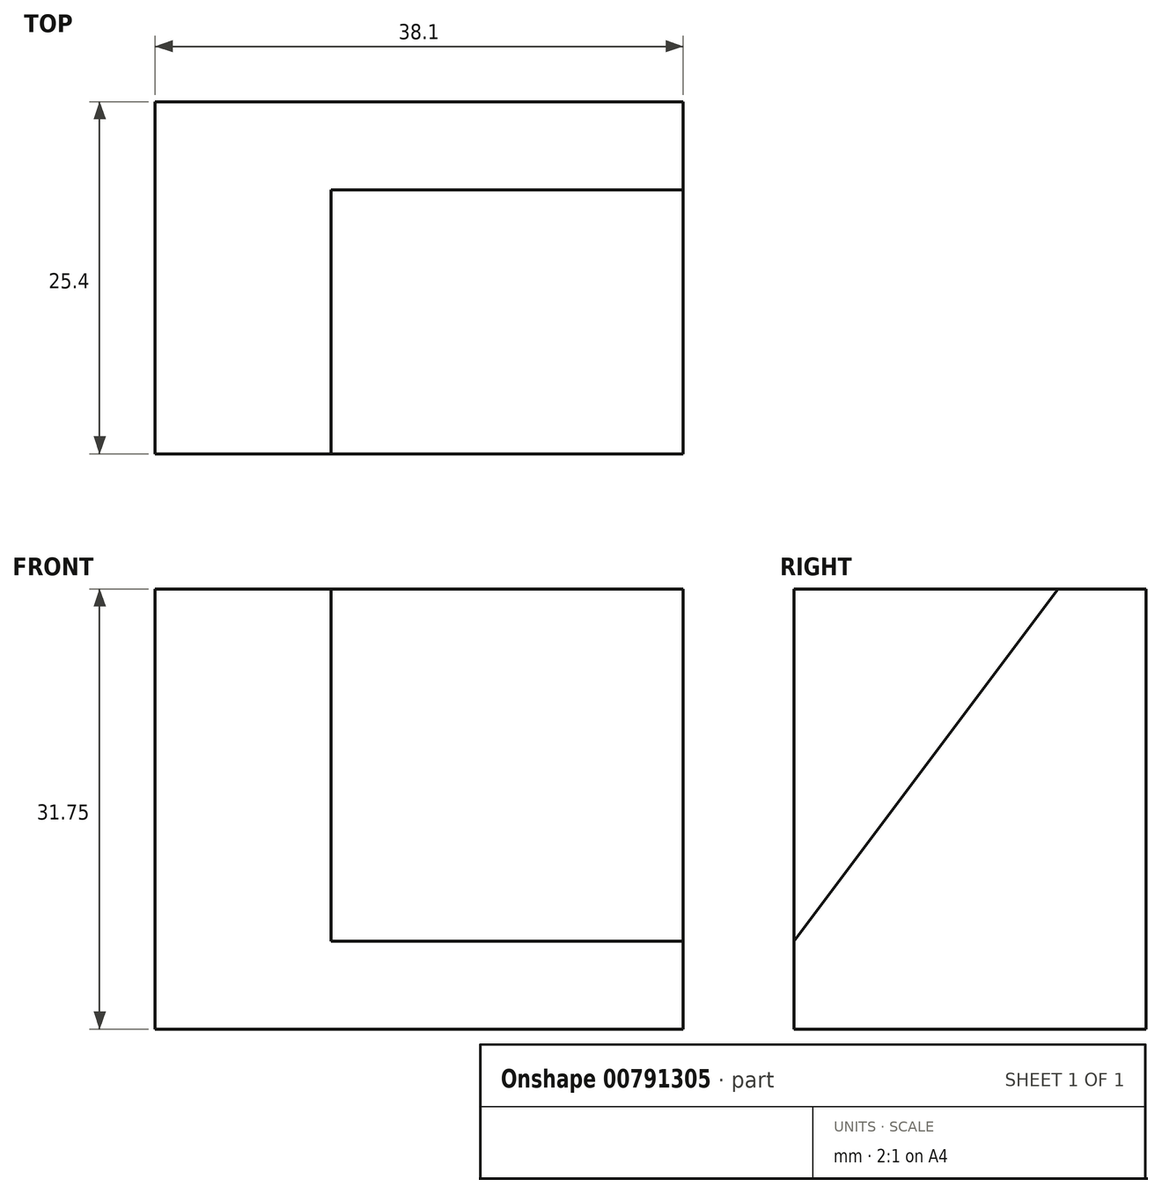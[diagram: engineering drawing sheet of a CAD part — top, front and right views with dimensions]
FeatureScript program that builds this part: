
annotation { "Feature Type Name" : "Feature", "Feature Type Description" : "" }
export const myFeature = defineFeature(function(context is Context, id is Id, definition is map)
    precondition{}
    {
        {
            var Q0;
            Q0=qCreatedBy(makeId("Front.planeOp"),FACE);
            var sketch = newSketch(context, id + "F0", { "sketchPlane" : qUnion([Q0])});
            skLineSegment(sketch, "E0", {"start": v(0, 0) * mm, "end": v(38.1, 0) * mm});
            skLineSegment(sketch, "E1", {"start": v(38.1, 0) * mm, "end": v(38.1, 31.75) * mm});
            skLineSegment(sketch, "E2", {"start": v(38.1, 31.75) * mm, "end": v(0, 31.75) * mm});
            skLineSegment(sketch, "E3", {"start": v(0, 31.75) * mm, "end": v(0, 0) * mm});
            skSolve(sketch);
        }
        {
            var Q0;
            Q0 = qSketchRegion(id + "F0", true);
            extrude(context, id + "F1", {"entities" : qUnion([Q0]), "depth" : 25.4 * mm, "offsetDistance" : 25.4 * mm});
        }
        {
            var Q0;
            Q0=makeQuery(id+"F1.opExtrude","SWEPT_FACE",FACE,{"disambiguationData":[OSD([sQuery(id+"F0.wireOp",EDGE,"E1")])]});
            var sketch = newSketch(context, id + "F2", { "sketchPlane" : qUnion([Q0])});
            skLineSegment(sketch, "E4", {"start": v(-25.4, 0) * mm, "end": v(-25.4, 6.35) * mm, "construction": true});
            skLineSegment(sketch, "E5", {"start": v(0, 31.75) * mm, "end": v(-6.35, 31.75) * mm, "construction": true});
            skLineSegment(sketch, "E6", {"start": v(-6.35, 31.75) * mm, "end": v(-25.4, 6.35) * mm});
            skSolve(sketch);
        }
        {
            var Q0;
            Q0 = qSketchRegion(id + "F2", true);
            var Q1;
            {var subQ0=sQuery(id+"F2.wireOp",EDGE,"E6");Q1=makeQuery(id+"F2.imprint","IMPRINT",FACE,{"disambiguationData":[TD([[makeQuery(id+"F2.imprint","IMPRINT",EDGE,{"derivedFrom":subQ0}),-1.0]])]});}
            extrude(context, id + "F3", {"entities" : qUnion([Q0, Q1]), "operationType" : NewBodyOperationType.REMOVE, "oppositeDirection" : true, "depth" : 25.4 * mm, "offsetDistance" : 25.4 * mm});
        }
    });
